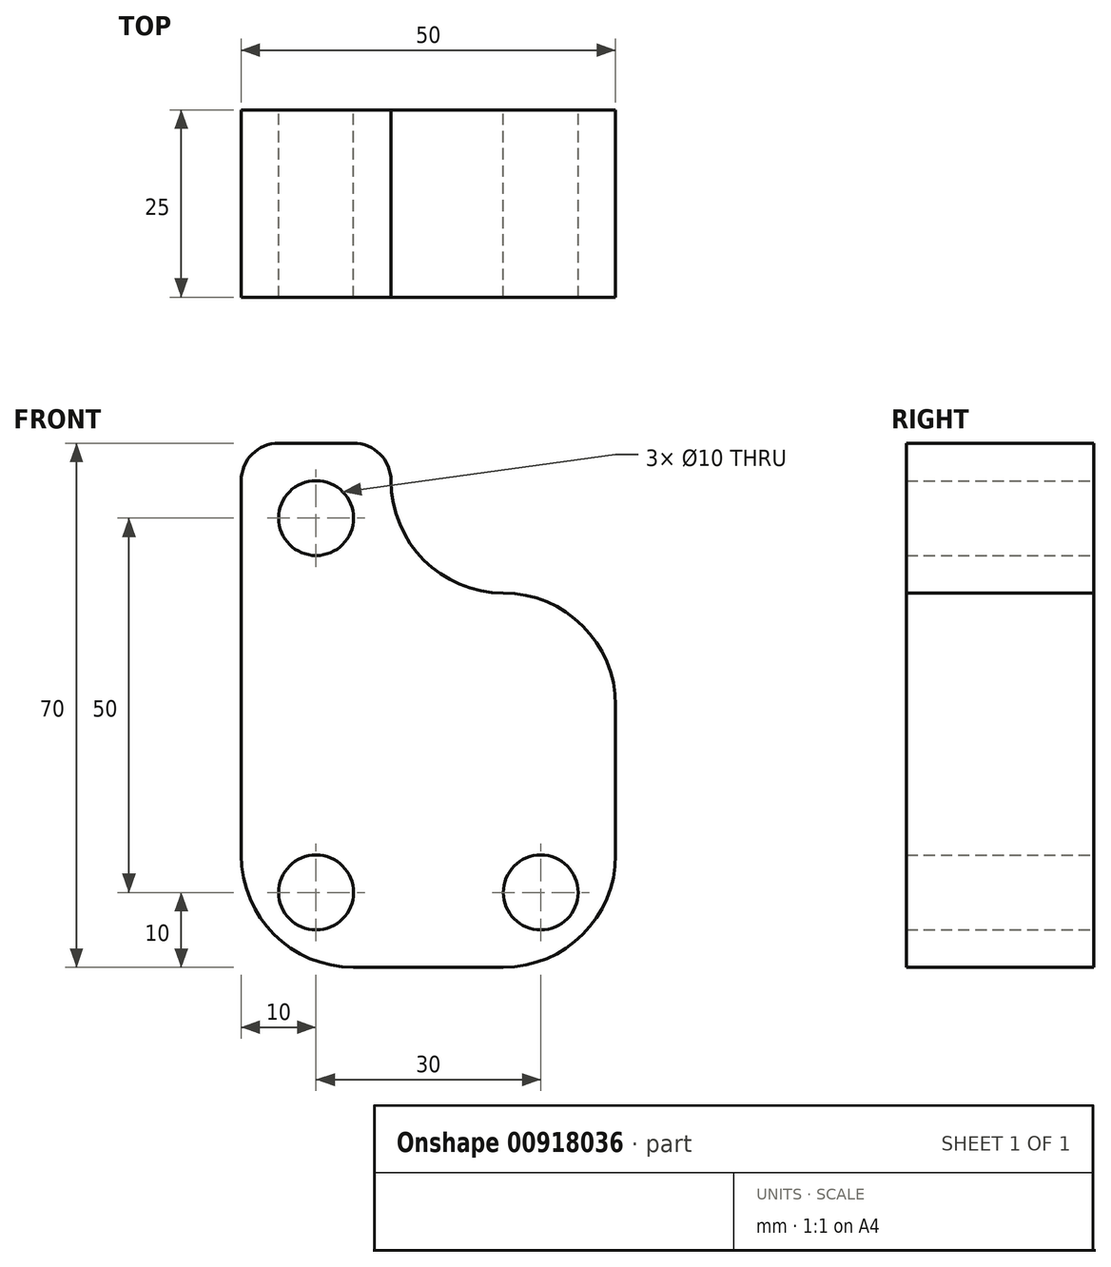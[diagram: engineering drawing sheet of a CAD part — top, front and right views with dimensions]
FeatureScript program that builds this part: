
annotation { "Feature Type Name" : "Feature", "Feature Type Description" : "" }
export const myFeature = defineFeature(function(context is Context, id is Id, definition is map)
    precondition{}
    {
        {
            var Q0;
            Q0=qCreatedBy(makeId("Front.planeOp"),FACE);
            var sketch = newSketch(context, id + "F0", { "sketchPlane" : qUnion([Q0])});
            skLineSegment(sketch, "E0", {"start": v(15, 0) * mm, "end": v(35, 0) * mm});
            skLineSegment(sketch, "E1", {"start": v(50, 15) * mm, "end": v(50, 35) * mm});
            skLineSegment(sketch, "E2", {"start": v(35, 50) * mm, "end": v(35, 50) * mm});
            skLineSegment(sketch, "E3", {"start": v(20, 65) * mm, "end": v(20, 65) * mm});
            skLineSegment(sketch, "E4", {"start": v(15, 70) * mm, "end": v(5, 70) * mm});
            skLineSegment(sketch, "E5", {"start": v(0, 65) * mm, "end": v(0, 15) * mm});
            skCircle(sketch, "E6", {"center": v(10, 60) * mm, "radius": 5 * mm});
            skCircle(sketch, "E7", {"center": v(10, 10) * mm, "radius": 5 * mm});
            skCircle(sketch, "E8", {"center": v(40, 10) * mm, "radius": 5 * mm});
            skPoint(sketch, "E9.visualSharp", {"position": v(20, 50) * mm});
            skArc(sketch, "E9.filletArc", {"start": v(20, 65) * mm, "mid": v(24.4, 54.4) * mm, "end": v(35, 50) * mm});
            skPoint(sketch, "E10.visualSharp", {"position": v(50, 50) * mm});
            skArc(sketch, "E10.filletArc", {"start": v(50, 35) * mm, "mid": v(45.6, 45.6) * mm, "end": v(35, 50) * mm});
            skPoint(sketch, "E11.visualSharp", {"position": v(50, 0) * mm});
            skArc(sketch, "E11.filletArc", {"start": v(35, 0) * mm, "mid": v(45.6, 4.4) * mm, "end": v(50, 15) * mm});
            skPoint(sketch, "E12.visualSharp", {"position": v(0, 0) * mm});
            skArc(sketch, "E12.filletArc", {"start": v(0, 15) * mm, "mid": v(4.4, 4.4) * mm, "end": v(15, 0) * mm});
            skPoint(sketch, "E13.visualSharp", {"position": v(0, 70) * mm});
            skArc(sketch, "E13.filletArc", {"start": v(5, 70) * mm, "mid": v(1.46, 68.54) * mm, "end": v(0, 65) * mm});
            skPoint(sketch, "E14.visualSharp", {"position": v(20, 70) * mm});
            skArc(sketch, "E14.filletArc", {"start": v(20, 65) * mm, "mid": v(18.54, 68.54) * mm, "end": v(15, 70) * mm});
            skSolve(sketch);
        }
        {
            var Q0;
            Q0=makeQuery(id+"F0.imprint","IMPRINT",FACE,{"disambiguationData":[TD([[makeQuery(id+"F0.imprint","IMPRINT",EDGE,{"derivedFrom":sQuery(id+"F0.wireOp",EDGE,"E0")}),1.0]])]});
            extrude(context, id + "F1", {"entities" : qUnion([Q0]), "depth" : 25 * mm, "offsetDistance" : 25 * mm});
        }
    });
